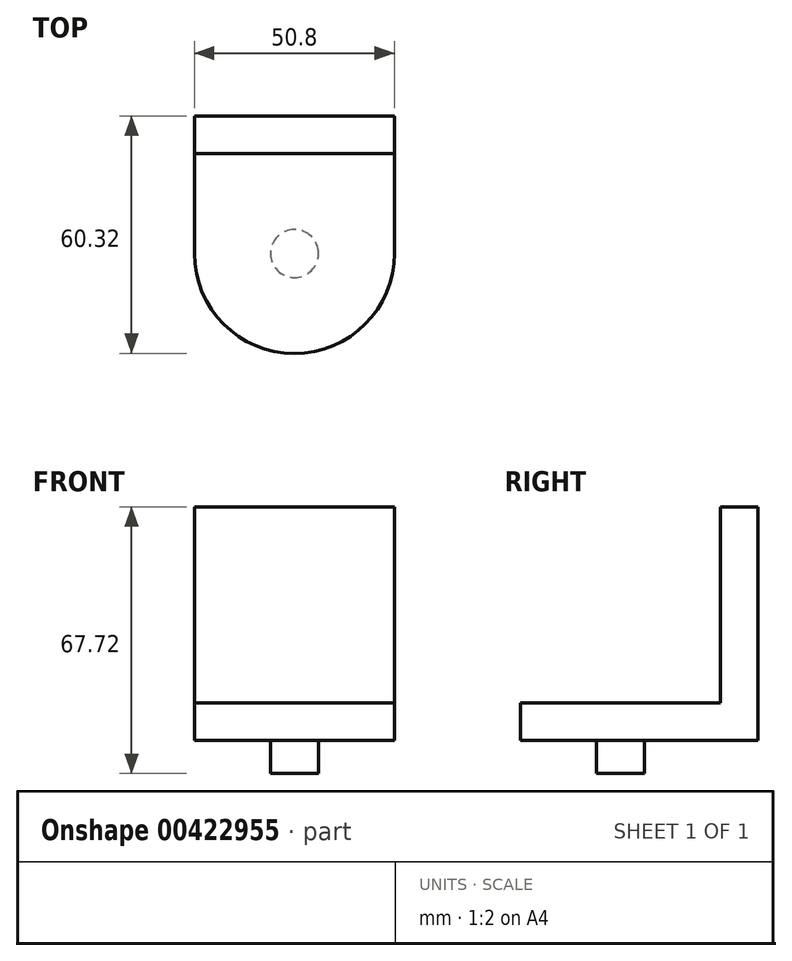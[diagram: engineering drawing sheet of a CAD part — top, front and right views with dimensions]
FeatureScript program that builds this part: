
annotation { "Feature Type Name" : "Feature", "Feature Type Description" : "" }
export const myFeature = defineFeature(function(context is Context, id is Id, definition is map)
    precondition{}
    {
        {
            var Q0;
            Q0=qCreatedBy(makeId("Top.planeOp"),FACE);
            var sketch = newSketch(context, id + "F0", { "sketchPlane" : qUnion([Q0])});
            skPoint(sketch, "E0.middle", {"position": v(0, 0) * mm});
            skLineSegment(sketch, "E1", {"start": v(-25.4, 25.4) * mm, "end": v(25.4, 25.4) * mm});
            skLineSegment(sketch, "E2", {"start": v(25.4, 25.4) * mm, "end": v(25.4, 0) * mm});
            skLineSegment(sketch, "E3", {"start": v(-25.4, 0) * mm, "end": v(-25.4, 25.4) * mm});
            skLineSegment(sketch, "E4", {"start": v(-25.4, 34.93) * mm, "end": v(25.4, 34.93) * mm});
            skLineSegment(sketch, "E5", {"start": v(25.4, 25.4) * mm, "end": v(25.4, 34.93) * mm});
            skLineSegment(sketch, "E6", {"start": v(-25.4, 34.93) * mm, "end": v(-25.4, 25.4) * mm});
            skArc(sketch, "E7", {"start": v(-25.4, 0) * mm, "mid": v(0, -25.4) * mm, "end": v(25.4, 0) * mm});
            skSolve(sketch);
        }
        {
            var Q0;
            Q0=makeQuery(id+"F0.imprint","IMPRINT",FACE,{"disambiguationData":[TD([[makeQuery(id+"F0.imprint","IMPRINT",EDGE,{"derivedFrom":sQuery(id+"F0.wireOp",EDGE,"E1")}),-1.0]])]});
            extrude(context, id + "F1", {"entities" : qUnion([Q0]), "depth" : 9.52 * mm, "offsetDistance" : 25.4 * mm});
        }
        {
            var Q0;
            Q0=makeQuery(id+"F0.imprint","IMPRINT",FACE,{"disambiguationData":[TD([[makeQuery(id+"F0.imprint","IMPRINT",EDGE,{"derivedFrom":sQuery(id+"F0.wireOp",EDGE,"E1")}),1.0]])]});
            extrude(context, id + "F2", {"entities" : qUnion([Q0]), "operationType" : NewBodyOperationType.ADD, "depth" : 59.26 * mm, "offsetDistance" : 25.4 * mm});
        }
        {
            var Q0;
            Q0=makeQuery(id+"F0.imprint","IMPRINT",FACE,{"disambiguationData":[TD([[makeQuery(id+"F0.imprint","IMPRINT",EDGE,{"derivedFrom":sQuery(id+"F0.wireOp",EDGE,"E1")}),-1.0]])]});
            var sketch = newSketch(context, id + "F3", { "sketchPlane" : qUnion([Q0])});
            skCircle(sketch, "E8", {"center": v(0, 0) * mm, "radius": 6.1 * mm});
            skSolve(sketch);
        }
        {
            var Q0;
            Q0=makeQuery(id+"F3.imprint","IMPRINT",FACE,{"disambiguationData":[TD([[makeQuery(id+"F3.imprint","IMPRINT",EDGE,{"derivedFrom":sQuery(id+"F3.wireOp",EDGE,"E8")}),1.0]])]});
            extrude(context, id + "F4", {"entities" : qUnion([Q0]), "operationType" : NewBodyOperationType.ADD, "oppositeDirection" : true, "depth" : 8.46 * mm, "offsetDistance" : 25.4 * mm});
        }
    });
